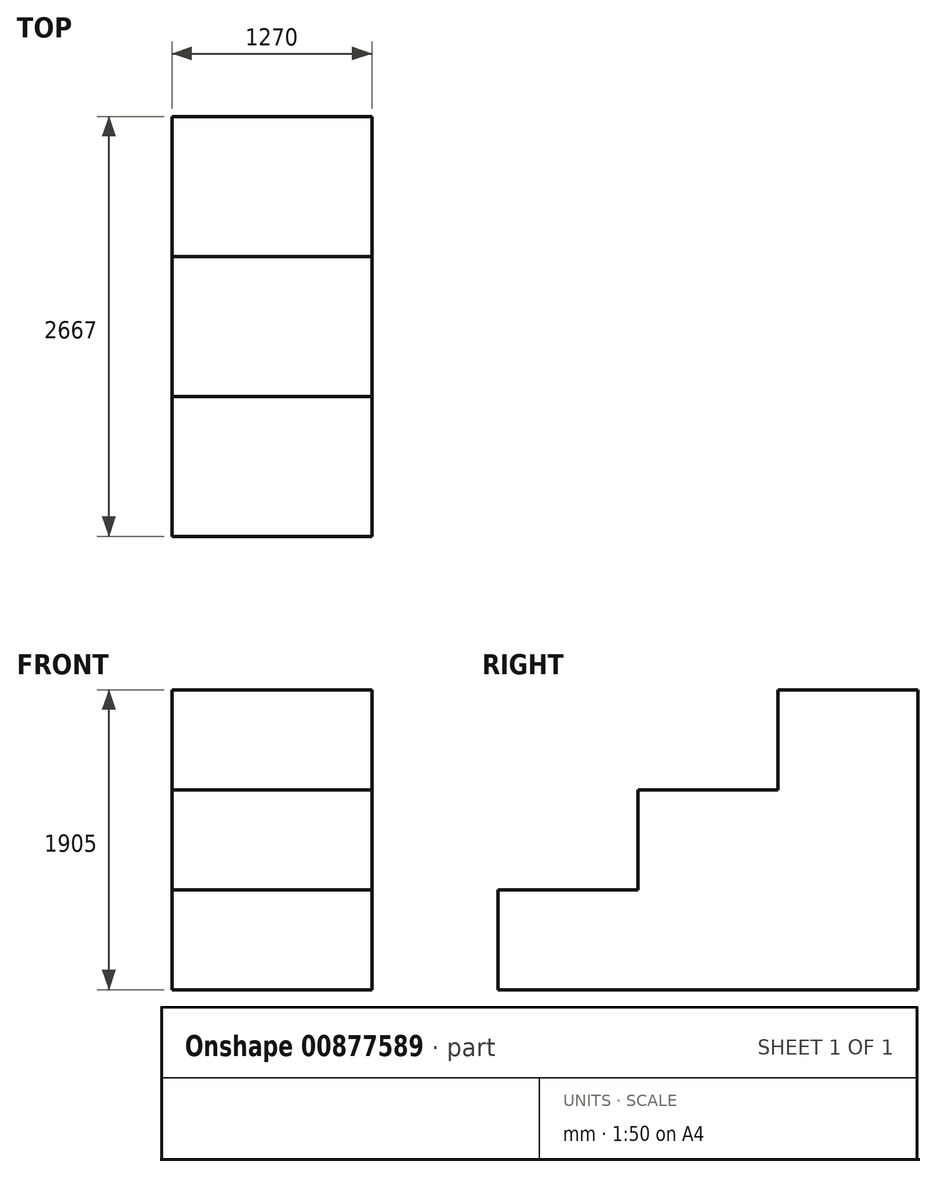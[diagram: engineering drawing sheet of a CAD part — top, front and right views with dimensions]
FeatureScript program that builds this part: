
annotation { "Feature Type Name" : "Feature", "Feature Type Description" : "" }
export const myFeature = defineFeature(function(context is Context, id is Id, definition is map)
    precondition{}
    {
        {
            var Q0;
            Q0=qCreatedBy(makeId("Right.planeOp"),FACE);
            var sketch = newSketch(context, id + "F0", { "sketchPlane" : qUnion([Q0])});
            skLineSegment(sketch, "E0", {"start": v(-73.65, -64.8) * mm, "end": v(2593.35, -64.8) * mm});
            skLineSegment(sketch, "E1", {"start": v(2593.35, -64.8) * mm, "end": v(2593.35, 1840.2) * mm});
            skLineSegment(sketch, "E2", {"start": v(2593.35, 1840.2) * mm, "end": v(1704.35, 1840.2) * mm});
            skLineSegment(sketch, "E3", {"start": v(1704.35, 1840.2) * mm, "end": v(1704.35, 1205.2) * mm});
            skLineSegment(sketch, "E4", {"start": v(1704.35, 1205.2) * mm, "end": v(815.35, 1205.2) * mm});
            skLineSegment(sketch, "E5", {"start": v(815.35, 1205.2) * mm, "end": v(815.35, 570.2) * mm});
            skLineSegment(sketch, "E6", {"start": v(815.35, 570.2) * mm, "end": v(-73.65, 570.2) * mm});
            skLineSegment(sketch, "E7", {"start": v(-73.65, 570.2) * mm, "end": v(-73.65, -64.8) * mm});
            skSolve(sketch);
        }
        {
            var Q0;
            Q0=makeQuery(id+"F0.imprint","IMPRINT",FACE,{"disambiguationData":[TD([[makeQuery(id+"F0.imprint","IMPRINT",EDGE,{"derivedFrom":sQuery(id+"F0.wireOp",EDGE,"E0")}),1.0]])]});
            extrude(context, id + "F1", {"entities" : qUnion([Q0]), "depth" : 1270 * mm, "offsetDistance" : 25.4 * mm});
        }
    });
